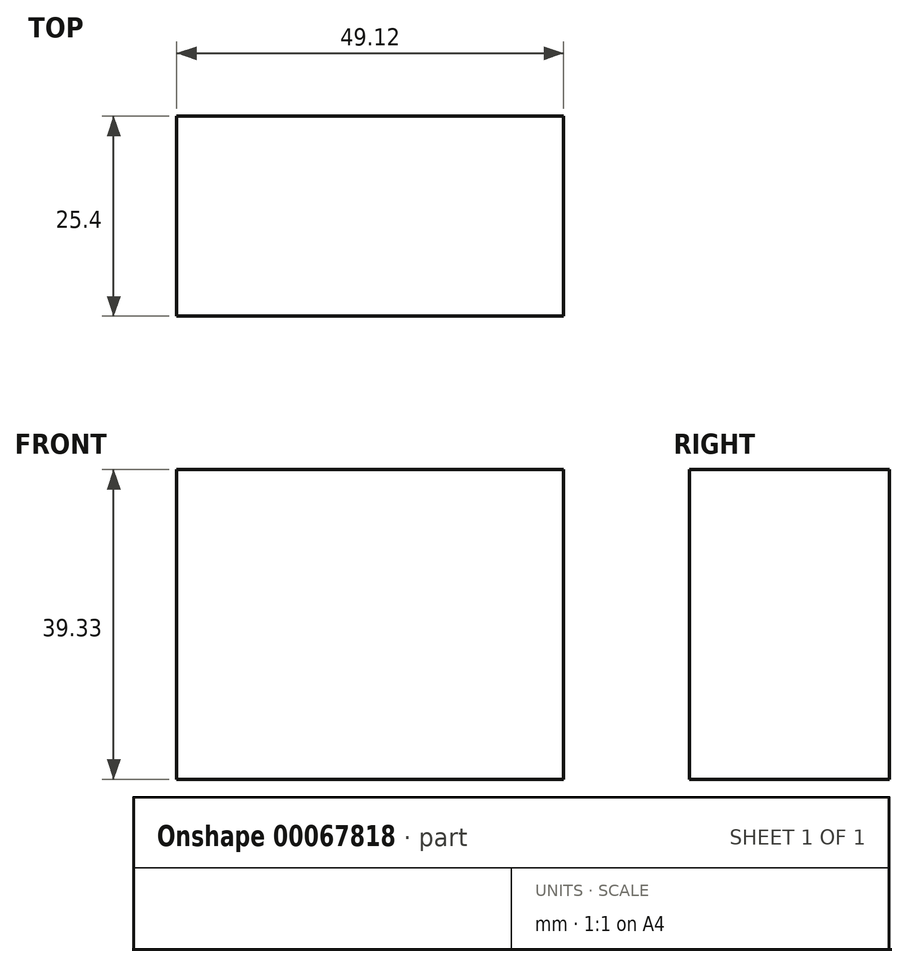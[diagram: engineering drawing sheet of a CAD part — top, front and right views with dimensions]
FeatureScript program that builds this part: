
annotation { "Feature Type Name" : "Feature", "Feature Type Description" : "" }
export const myFeature = defineFeature(function(context is Context, id is Id, definition is map)
    precondition{}
    {
        {
            var Q0;
            Q0=qCreatedBy(makeId("Front.planeOp"),FACE);
            var sketch = newSketch(context, id + "F0", { "sketchPlane" : qUnion([Q0])});
            skLineSegment(sketch, "E0.bottom", {"start": v(0, 0) * mm, "end": v(49.12, 0) * mm});
            skLineSegment(sketch, "E0.top", {"start": v(0, 39.33) * mm, "end": v(49.12, 39.33) * mm});
            skLineSegment(sketch, "E0.left", {"start": v(0, 0) * mm, "end": v(0, 39.33) * mm});
            skLineSegment(sketch, "E0.right", {"start": v(49.12, 0) * mm, "end": v(49.12, 39.33) * mm});
            skSolve(sketch);
        }
        {
            var Q0;
            Q0=makeQuery(id+"F0.imprint","IMPRINT",FACE,{"disambiguationData":[TD([[makeQuery(id+"F0.imprint","IMPRINT",EDGE,{"derivedFrom":sQuery(id+"F0.wireOp",EDGE,"E0.bottom")}),1.0]])]});
            extrude(context, id + "F1", {"entities" : qUnion([Q0]), "endBound" : BoundingType.SYMMETRIC, "depth" : 25.4 * mm, "offsetDistance" : 25.4 * mm});
        }
    });
